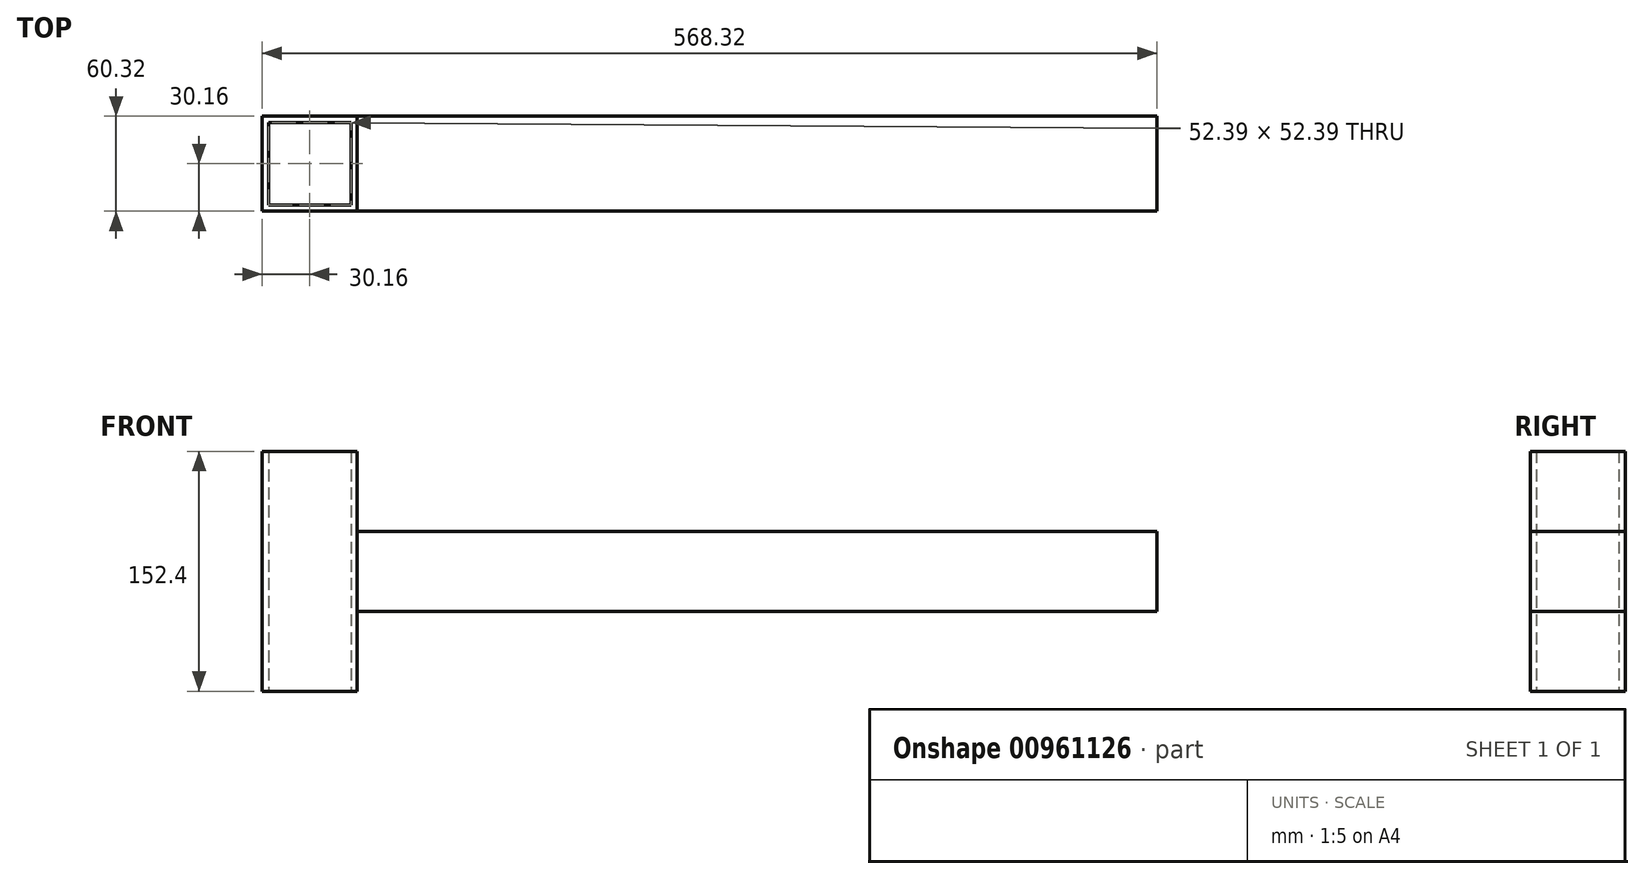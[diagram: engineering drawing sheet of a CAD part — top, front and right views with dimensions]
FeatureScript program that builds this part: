
annotation { "Feature Type Name" : "Feature", "Feature Type Description" : "" }
export const myFeature = defineFeature(function(context is Context, id is Id, definition is map)
    precondition{}
    {
        {
            var Q0;
            Q0=qCreatedBy(makeId("Top.planeOp"),FACE);
            var sketch = newSketch(context, id + "F0", { "sketchPlane" : qUnion([Q0])});
            skLineSegment(sketch, "E0.bottom", {"start": v(-26.2, 26.2) * mm, "end": v(26.2, 26.2) * mm});
            skLineSegment(sketch, "E0.top", {"start": v(-26.2, -26.2) * mm, "end": v(26.2, -26.2) * mm});
            skLineSegment(sketch, "E0.left", {"start": v(-26.2, 26.2) * mm, "end": v(-26.2, -26.2) * mm});
            skLineSegment(sketch, "E0.right", {"start": v(26.2, 26.2) * mm, "end": v(26.2, -26.2) * mm});
            skPoint(sketch, "E0.middle", {"position": v(0, 0) * mm});
            skLineSegment(sketch, "E1.bottom", {"start": v(-30.16, 30.16) * mm, "end": v(30.16, 30.16) * mm});
            skLineSegment(sketch, "E1.top", {"start": v(-30.16, -30.16) * mm, "end": v(30.16, -30.16) * mm});
            skLineSegment(sketch, "E1.left", {"start": v(-30.16, 30.16) * mm, "end": v(-30.16, -30.16) * mm});
            skLineSegment(sketch, "E1.right", {"start": v(30.16, 30.16) * mm, "end": v(30.16, -30.16) * mm});
            skSolve(sketch);
        }
        {
            var Q0;
            Q0 = qSketchRegion(id + "F0", true);
            extrude(context, id + "F1", {"entities" : qUnion([Q0]), "depth" : 152.4 * mm, "offsetDistance" : 25.4 * mm});
        }
        {
            var Q0;
            Q0=makeQuery(id+"F1.opExtrude","SWEPT_FACE",FACE,{"disambiguationData":[OSD([sQuery(id+"F0.wireOp",EDGE,"E1.top")])]});
            var sketch = newSketch(context, id + "F2", { "sketchPlane" : qUnion([Q0])});
            skLineSegment(sketch, "E2.bottom", {"start": v(30.16, 101.6) * mm, "end": v(538.16, 101.6) * mm});
            skLineSegment(sketch, "E2.top", {"start": v(30.16, 50.8) * mm, "end": v(538.16, 50.8) * mm});
            skLineSegment(sketch, "E2.left", {"start": v(30.16, 101.6) * mm, "end": v(30.16, 50.8) * mm});
            skLineSegment(sketch, "E2.right", {"start": v(538.16, 101.6) * mm, "end": v(538.16, 50.8) * mm});
            skSolve(sketch);
        }
        {
            var Q0;
            Q0=makeQuery(id+"F2.imprint","IMPRINT",FACE,{"disambiguationData":[TD([[makeQuery(id+"F2.imprint","IMPRINT",EDGE,{"derivedFrom":sQuery(id+"F2.wireOp",EDGE,"E2.bottom")}),-1.0]])]});
            extrude(context, id + "F3", {"entities" : qUnion([Q0]), "oppositeDirection" : true, "depth" : 60.32 * mm, "offsetDistance" : 25.4 * mm});
        }
    });
